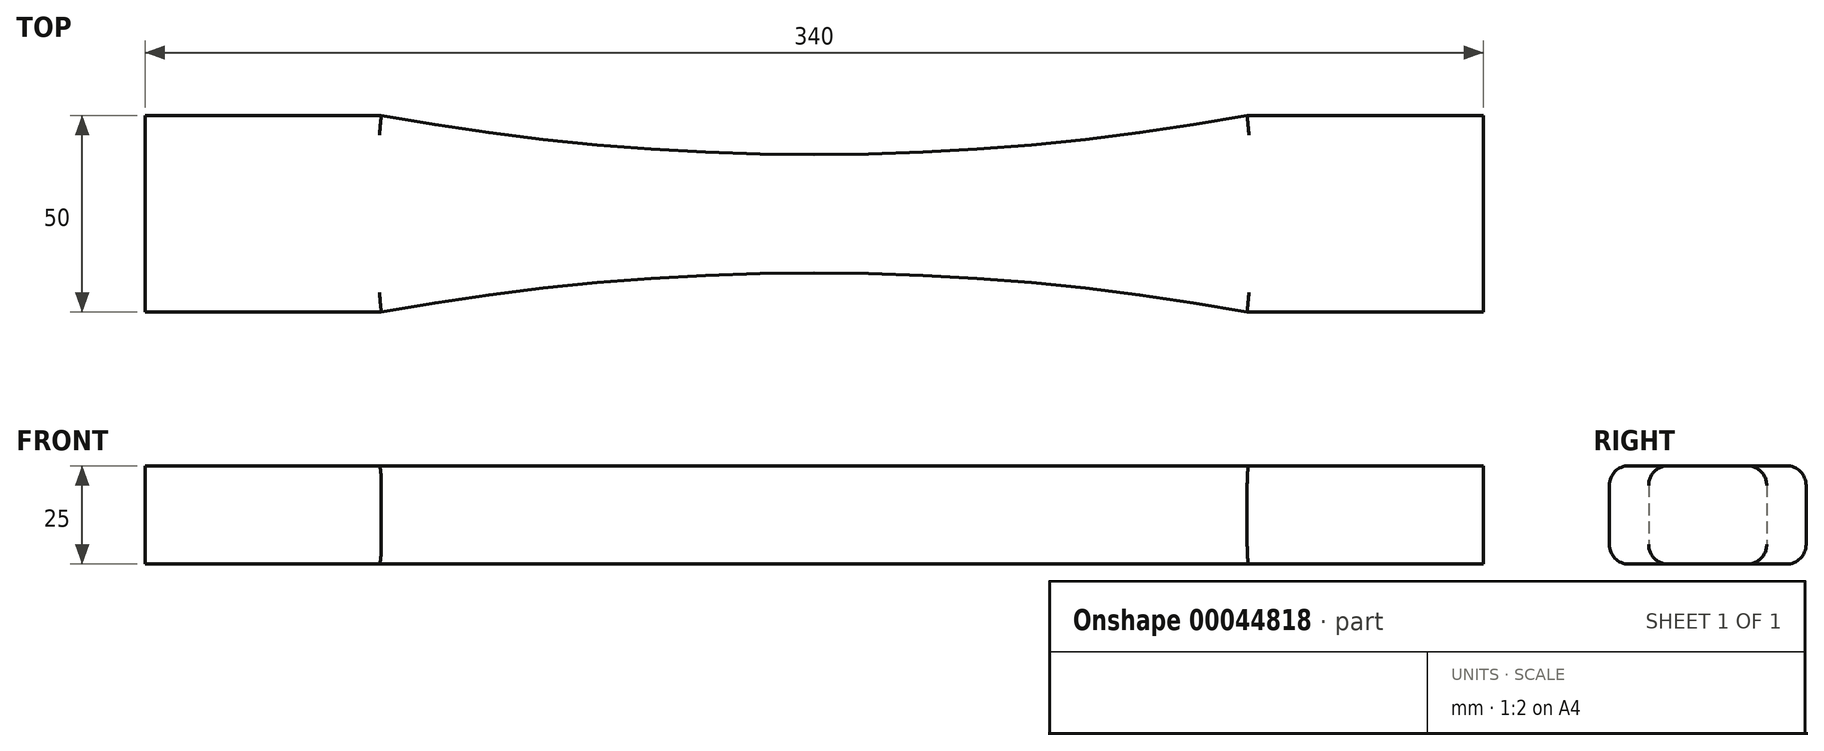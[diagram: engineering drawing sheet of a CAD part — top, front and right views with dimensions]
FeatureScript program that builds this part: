
annotation { "Feature Type Name" : "Feature", "Feature Type Description" : "" }
export const myFeature = defineFeature(function(context is Context, id is Id, definition is map)
    precondition{}
    {
        {
            var Q0;
            Q0=qCreatedBy(makeId("Top.planeOp"),FACE);
            var sketch = newSketch(context, id + "F0", { "sketchPlane" : qUnion([Q0])});
            skLineSegment(sketch, "E0.rect.bottom", {"start": v(-170, -25) * mm, "end": v(-110, -25) * mm});
            skLineSegment(sketch, "E0.rect.top", {"start": v(-170, 25) * mm, "end": v(-110, 25) * mm});
            skLineSegment(sketch, "E0.rect.left", {"start": v(-170, -25) * mm, "end": v(-170, 25) * mm});
            skLineSegment(sketch, "E0.rect.right", {"start": v(170, -25) * mm, "end": v(170, 25) * mm});
            skPoint(sketch, "E0.rect.middle", {"position": v(0, 0) * mm});
            skLineSegment(sketch, "E1", {"start": v(-54.44, -189.72) * mm, "end": v(71.67, -189.72) * mm});
            skLineSegment(sketch, "E2", {"start": v(0, -171.39) * mm, "end": v(0, -198.61) * mm});
            skLineSegment(sketch, "E3", {"start": v(-110, 25) * mm, "end": v(-110, -25) * mm});
            skLineSegment(sketch, "E4", {"start": v(110, 25) * mm, "end": v(110, -25) * mm});
            skArc(sketch, "E5", {"start": v(110, -25) * mm, "mid": v(0, -15) * mm, "end": v(-110, -25) * mm});
            skLineSegment(sketch, "E6.trimOffspring", {"start": v(110, -25) * mm, "end": v(170, -25) * mm});
            skPoint(sketch, "E7.endSnap0", {"position": v(170, 0) * mm});
            skArc(sketch, "E8.MirrorCS", {"start": v(110, 25) * mm, "mid": v(0, 15) * mm, "end": v(-110, 25) * mm});
            skLineSegment(sketch, "E9.trimOffspring", {"start": v(110, 25) * mm, "end": v(170, 25) * mm});
            skSolve(sketch);
        }
        {
            var Q0;
            Q0 = qSketchRegion(id + "F0", true);
            extrude(context, id + "F1", {"entities" : qUnion([Q0]), "depth" : 25 * mm});
        }
        {
            var Q0;
            Q0=makeQuery(id+"F1.opExtrude","CAP_EDGE",EDGE,{"disambiguationData":[OSD([sQuery(id+"F0.wireOp",EDGE,"E0.rect.bottom")])],"isStart":false});
            var Q1;
            Q1=makeQuery(id+"F1.opExtrude","CAP_EDGE",EDGE,{"disambiguationData":[OSD([sQuery(id+"F0.wireOp",EDGE,"E5")])],"isStart":false});
            var Q2;
            Q2=makeQuery(id+"F1.opExtrude","CAP_EDGE",EDGE,{"disambiguationData":[OSD([sQuery(id+"F0.wireOp",EDGE,"E6.trimOffspring")])],"isStart":false});
            var Q3;
            Q3=makeQuery(id+"F1.opExtrude","CAP_EDGE",EDGE,{"disambiguationData":[OSD([sQuery(id+"F0.wireOp",EDGE,"E9.trimOffspring")])],"isStart":false});
            var Q4;
            Q4=makeQuery(id+"F1.opExtrude","CAP_EDGE",EDGE,{"disambiguationData":[OSD([sQuery(id+"F0.wireOp",EDGE,"E8.MirrorCS")])],"isStart":false});
            var Q5;
            Q5=makeQuery(id+"F1.opExtrude","CAP_EDGE",EDGE,{"disambiguationData":[OSD([sQuery(id+"F0.wireOp",EDGE,"E0.rect.top")])],"isStart":false});
            var Q6;
            Q6=makeQuery(id+"F1.opExtrude","CAP_EDGE",EDGE,{"disambiguationData":[OSD([sQuery(id+"F0.wireOp",EDGE,"E0.rect.bottom")])],"isStart":true});
            var Q7;
            Q7=makeQuery(id+"F1.opExtrude","CAP_EDGE",EDGE,{"disambiguationData":[OSD([sQuery(id+"F0.wireOp",EDGE,"E5")])],"isStart":true});
            var Q8;
            Q8=makeQuery(id+"F1.opExtrude","CAP_EDGE",EDGE,{"disambiguationData":[OSD([sQuery(id+"F0.wireOp",EDGE,"E6.trimOffspring")])],"isStart":true});
            var Q9;
            Q9=makeQuery(id+"F1.opExtrude","CAP_EDGE",EDGE,{"disambiguationData":[OSD([sQuery(id+"F0.wireOp",EDGE,"E0.rect.top")])],"isStart":true});
            var Q10;
            Q10=makeQuery(id+"F1.opExtrude","CAP_EDGE",EDGE,{"disambiguationData":[OSD([sQuery(id+"F0.wireOp",EDGE,"E8.MirrorCS")])],"isStart":true});
            var Q11;
            Q11=makeQuery(id+"F1.opExtrude","CAP_EDGE",EDGE,{"disambiguationData":[OSD([sQuery(id+"F0.wireOp",EDGE,"E9.trimOffspring")])],"isStart":true});
            fillet(context, id + "F2", {"entities" : qUnion([Q0, Q1, Q2, Q3, Q4, Q5, Q6, Q7, Q8, Q9, Q10, Q11]), "radius" : 5 * mm, "tangentPropagation" : true, "allowEdgeOverflow" : false});
        }
    });
